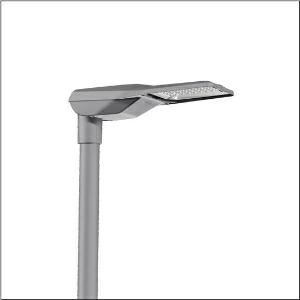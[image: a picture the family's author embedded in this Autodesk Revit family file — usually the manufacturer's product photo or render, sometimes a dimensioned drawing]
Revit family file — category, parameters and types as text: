
# Revit family: streetlight_sl_21_iq_mini___pl52_5xe2h41d08gb_a481
name_source: partatom
category: Lighting Fixtures
units: mm (PartAtom-declared; Revit-internal decimal feet)

## family parameters
Cut with Voids When Loaded = No
Host = Face
Light Source = No
Part Type = Normal
Room Calculation Point = No
Round Connector Dimension = Use Diameter
Shared = No

## types (1)
- --- (1 x LED, 5810 lm, 37.1 W, 4000K)
    Apparent Load = 37 VA
    CIE Flux Codes = 27 59 98 100 100
    Color Rendering = 70
    Color Temperature = 4000K
    Default Elevation = 1800 mm
    Description = Streetlight SL 21 iQ mini, mast luminaire, primary light control with lens, of PMMA, primary optical cover: cover, of toughened safety glass, transparent, light distribution: PL52, light emission: direct distribution, primary light characteristic: asymmetric, installation type: post-top, side-entry, LED, High Power LED, rated luminous flux: 5.810lm, luminous efficacy: 157lm/W, light colour: 740, colour temperature: 4000K, control: Auto-Match, Temp-Guard, Lumen-Switch, Night-Set, Smart-Wire, Light-Fading, Desk-Remote (wireless, voltage-free reading and setting of iQ features in the workshop via application-optimized NFC function/RFID function), optimised constant luminous flux control (CLO 2.0), presetting dimming linear, mains connection: 220..240V, AC, 50/60Hz, start of lifetime: 37W, end of service life: 39W, reduction: 18W, luminaire housing, of diecast aluminium, powder-coated, Siteco® metallic grey (DB 702S), corrosivity category C5 mid according to DIN EN ISO 12944, please order mast flange separately, inclination adjustable: 0°, 5°, 10°, 15°, sealing non-destructively replaceable, multi-level sealing system, length: 628mm, width: 235mm, height: 110mm, mast flange for spigot size: 42mm (side-entry): 5XC10008XM4, 60/48mm (side-entry/post-top): 5XC10108XM2, 76/60mm (side-entry/post-top): 5XC10108XM1, protection rating (complete): IP66, insulation class (complete): insulation class II (safety insulation), certification: CE, ENEC, ENEC+, VDE, impact resistance: IK09, permissible operating ambient temperature for outdoor applications: -40..+50°C, standard-compliant lighting for roads and squares, packaging unit: 1 piece

Light Distribution: PL52
    Height = 110 mm
    Lamp = 1 x LED
    Lamp Light Flux = 5810 lm
    Lamp Power = 37.1 W
    Lamp count = 1
    Length = 625 mm
    Luminous efficacy = 157 lm/W
    Manufacturer = Siteco
    ModVariant = No
    Model = 5XE2H41D08GB
    Number of Poles = 1
    OnlyDefault = Yes
    Power Factor = 1
    Product Name = Streetlight SL 21 iQ mini | PL52
    Product group = mast luminaire | pylon top
    ProductGroupID = 6100
    Protection Class = Protection class II
    Protection Degree = IP 66
    RLX_Detail_Level = 1
    RLX_Emergency_Light_Flux = 0 lm
    RLX_Emergency_Type = 0
    RLX_Emergency_Type_DB = No
    RlxData = <blob elided: 102025 chars, md5=21722781>
    Socket = socket
    Standby Power = 0 W
    System Light Flux = 5810 lm
    System Power = 37 W
    Type Comments = factory setting: luminous flux: 100 % | dim-lin: 254 | 385 mA
    Type Image = l_1003519.jpg
    URL = http://relux.com
    VarID = @adj_142605
    Voltage = 0 V
    Weight = 0.00 kg
    Width = 234 mm

## geometry (parser evidence)
native form markers: Blend x4, Sweep x9
no freeform markers — native parametric forms only
